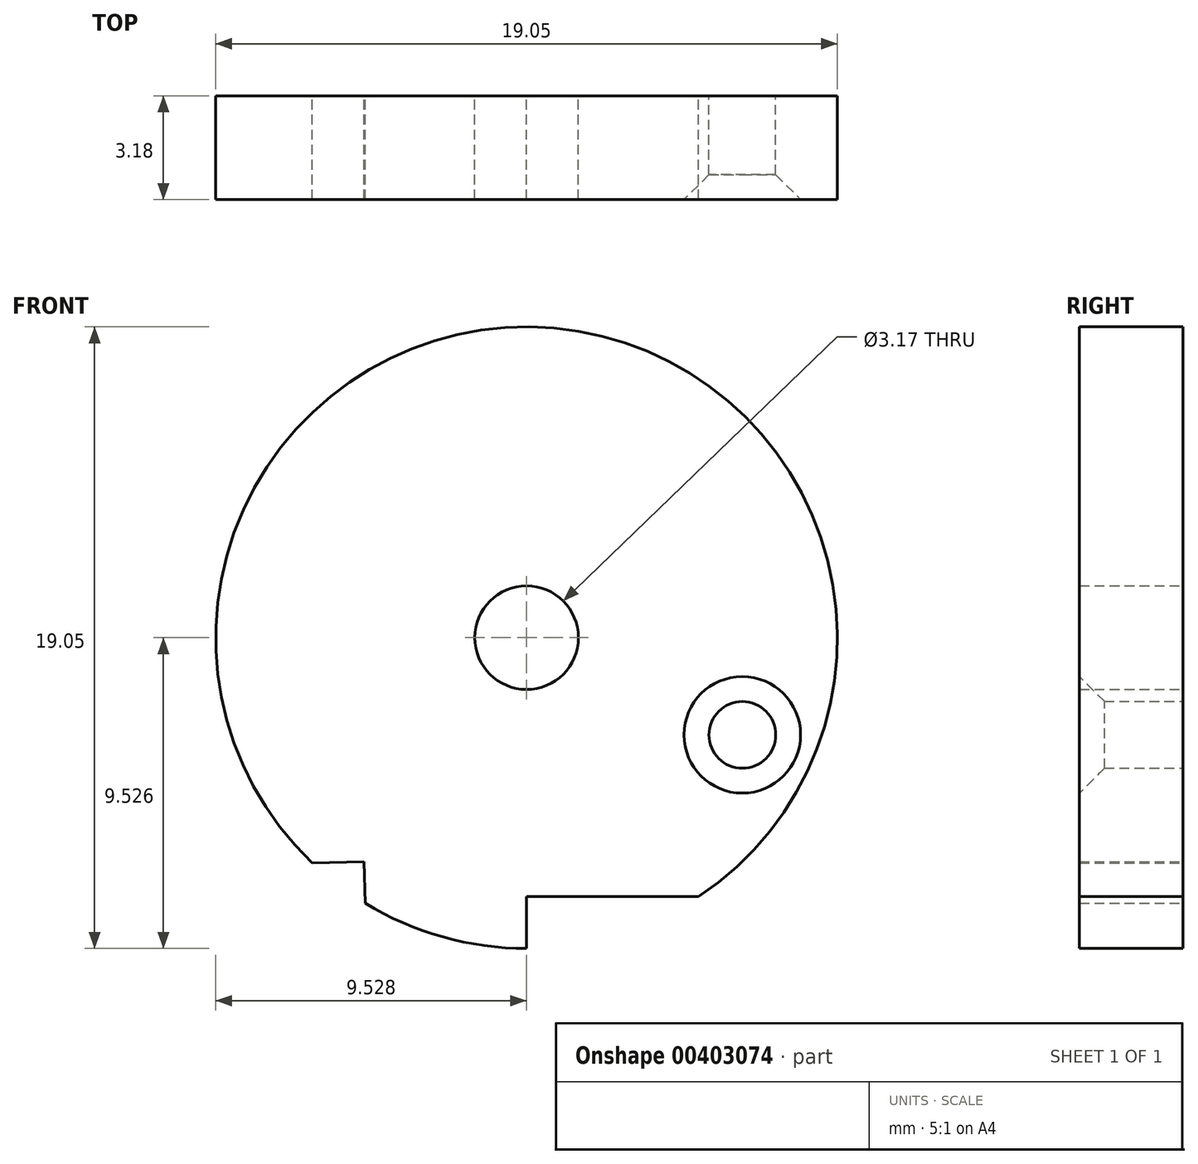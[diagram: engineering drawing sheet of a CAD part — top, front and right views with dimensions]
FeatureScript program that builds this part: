
annotation { "Feature Type Name" : "Feature", "Feature Type Description" : "" }
export const myFeature = defineFeature(function(context is Context, id is Id, definition is map)
    precondition{}
    {
        {
            var Q0;
            Q0=qCreatedBy(makeId("Front.planeOp"),FACE);
            var sketch = newSketch(context, id + "F0", { "sketchPlane" : qUnion([Q0])});
            skArc(sketch, "E0", {"start": v(-4.47, -3.05) * mm, "mid": v(-2.1, -4.09) * mm, "end": v(0.48, -4.44) * mm});
            skCircle(sketch, "E1", {"center": v(0.48, 5.09) * mm, "radius": 1.59 * mm});
            skLineSegment(sketch, "E2", {"start": v(-6.09, -1.81) * mm, "end": v(-4.5, -1.78) * mm});
            skLineSegment(sketch, "E3", {"start": v(-4.5, -1.78) * mm, "end": v(-4.47, -3.05) * mm});
            skCircle(sketch, "E4", {"center": v(7.09, 2.1) * mm, "radius": 1.02 * mm});
            skLineSegment(sketch, "E5", {"start": v(0.48, -2.85) * mm, "end": v(0.48, -4.44) * mm});
            skLineSegment(sketch, "E6", {"start": v(0.48, -2.85) * mm, "end": v(5.74, -2.85) * mm});
            skArc(sketch, "E7.trimOffspring", {"start": v(5.74, -2.85) * mm, "mid": v(1.31, 14.57) * mm, "end": v(-6.09, -1.81) * mm});
            skSolve(sketch);
        }
        {
            var Q0;
            Q0=makeQuery(id+"F0.imprint","IMPRINT",FACE,{"disambiguationData":[TD([[makeQuery(id+"F0.imprint","IMPRINT",EDGE,{"derivedFrom":sQuery(id+"F0.wireOp",EDGE,"E0")}),1.0]])]});
            extrude(context, id + "F1", {"entities" : qUnion([Q0]), "endBound" : BoundingType.SYMMETRIC, "depth" : 3.17 * mm});
        }
        {
            var Q0;
            Q0=makeQuery(id+"F1.opExtrude","CAP_EDGE",EDGE,{"disambiguationData":[OSD([sQuery(id+"F0.wireOp",EDGE,"E4")])],"isStart":false});
            chamfer(context, id + "F2", {"entities" : qUnion([Q0]), "chamferType" : ChamferType.TWO_OFFSETS, "width1" : 0.76 * mm, "oppositeDirection" : false, "width2" : 0.76 * mm, "tangentPropagation" : true});
        }
    });
